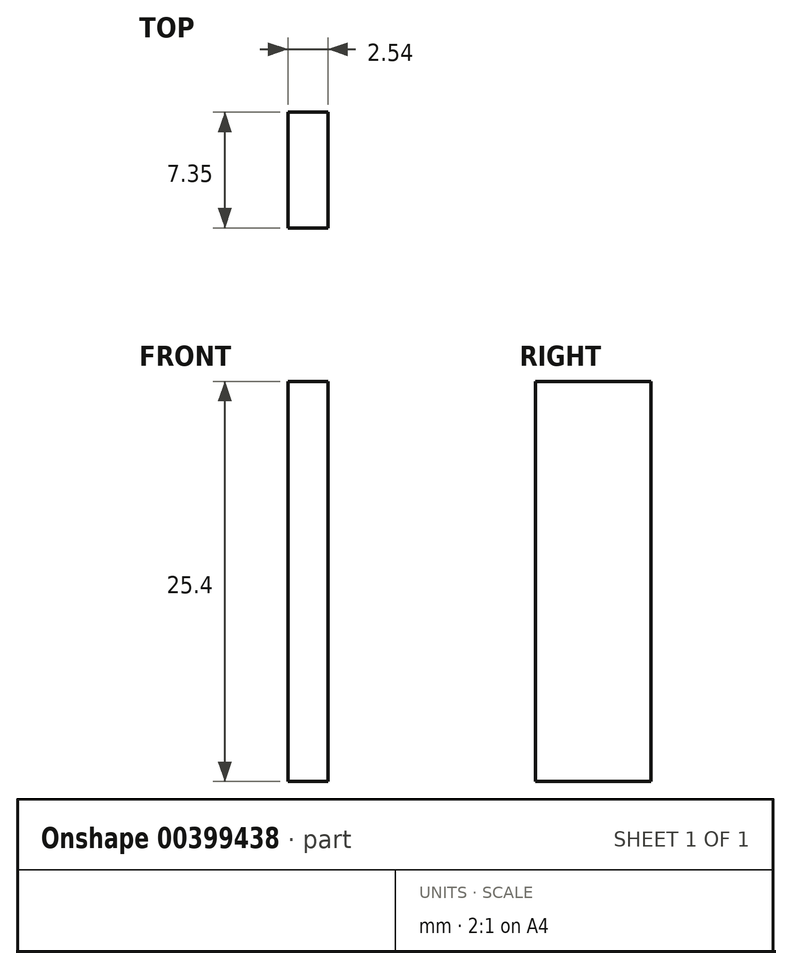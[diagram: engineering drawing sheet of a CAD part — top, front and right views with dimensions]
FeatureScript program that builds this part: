
annotation { "Feature Type Name" : "Feature", "Feature Type Description" : "" }
export const myFeature = defineFeature(function(context is Context, id is Id, definition is map)
    precondition{}
    {
        {
            var Q0;
            Q0=qCreatedBy(makeId("Top.planeOp"),FACE);
            var sketch = newSketch(context, id + "F0", { "sketchPlane" : qUnion([Q0])});
            skLineSegment(sketch, "E0.bottom", {"start": v(-46.75, 32.2) * mm, "end": v(-44.2, 32.2) * mm});
            skLineSegment(sketch, "E0.top", {"start": v(-46.75, 24.85) * mm, "end": v(-44.2, 24.85) * mm});
            skLineSegment(sketch, "E0.left", {"start": v(-46.75, 32.2) * mm, "end": v(-46.75, 24.85) * mm});
            skLineSegment(sketch, "E0.right", {"start": v(-44.2, 32.2) * mm, "end": v(-44.2, 24.85) * mm});
            skSolve(sketch);
        }
        {
            var Q0;
            Q0 = qSketchRegion(id + "F0", true);
            var Q1;
            Q1=sQuery(id+"F0.wireOp",EDGE,"E0.left");
            var Q2;
            Q2=sQuery(id+"F0.wireOp",EDGE,"E0.top");
            var Q3;
            Q3=sQuery(id+"F0.wireOp",EDGE,"E0.right");
            var Q4;
            Q4=sQuery(id+"F0.wireOp",EDGE,"E0.bottom");
            extrude(context, id + "F1", {"entities" : qUnion([Q0]), "bodyType" : ToolBodyType.SURFACE, "surfaceEntities" : qUnion([Q1, Q2, Q3, Q4]), "depth" : 25.4 * mm});
        }
    });
